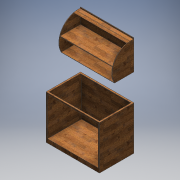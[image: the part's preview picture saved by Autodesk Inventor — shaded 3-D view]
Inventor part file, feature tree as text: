
AUTODESK INVENTOR PART (.ipt)
format: ipt  version: 2016 (Build 200138000, 138)  size: 333,312 bytes
history: native  units: mm
features: extrude x13, sketch x12, projected_geometry x9, plane x3
ambient origin geometry x8: Origin, YZ Plane, XZ Plane, XY Plane, X Axis, Y Axis, Z Axis, Center Point
bodies: Solid1 (feature_tree)
feature tree (37):
  extrude  "Extrusion1"  Depth=10.0mm
  extrude  "Extrusion2"  Depth=80.0mm
  extrude  "Extrusion3"  Depth=30.0mm
  extrude  "Extrusion4"  Depth=30.0mm
  plane  "Work Plane1"
  extrude  "Extrusion5"  Depth=10.0mm
  extrude  "Extrusion6"  Depth=10.0mm
  extrude  "Extrusion7"  Depth=10.0mm
  extrude  "Extrusion9"  TaperAngle=0.0deg  [1 undecoded]
  plane  "Work Plane2"
  extrude  "Extrusion11"  Depth=30.0mm
  extrude  "Extrusion13"  Depth=700.0mm TaperAngle=0.0deg
  plane  "Work Plane3"
  extrude  "Extrusion14"  TaperAngle=0.0deg  [1 undecoded]
  extrude  "Extrusion15"  Depth=10.0mm
  extrude  "Extrusion16"  TaperAngle=0.0deg  [1 undecoded]
  sketch  "Sketch1"  dims[d3=0.0mm d5=10.0mm]
  sketch  "Sketch2"  dims[d6=10.0mm d7=80.0mm]
  projected_geometry  "Projected Loop1"
  sketch  "Sketch3"  dims[d9=0.0mm d10=30.0mm]
  projected_geometry  "Projected Loop2"
  sketch  "Sketch4"  dims[d11=400.0mm d12=0.0mm d13=30.0mm]
  projected_geometry  "Projected Loop3"
  projected_geometry  "Projected Loop4"
  projected_geometry  "Projected Loop5"
  sketch  "Sketch5"  dims[d14=30.0mm d15=10.0mm]
  sketch  "Sketch6"  dims[d16=0.0mm d18=10.0mm]
  projected_geometry  "Projected Loop6"
  sketch  "Sketch7"  dims[d19=0.0mm d20=10.0mm]
  projected_geometry  "Projected Loop7"
  projected_geometry  "Projected Loop9"
  sketch  "Sketch12"  dims[d21=10.0mm d23=0.0mm]
  sketch  "Sketch14"  dims[d24=30.0mm d25=30.0mm]
  sketch  "Sketch15"  dims[d26=30.0mm d27=700.0mm d28=0.0mm]
  sketch  "Sketch16"  dims[d33=10.0mm d34=0.0mm]
  sketch  "Sketch17"  dims[d40=280.0mm d41=10.0mm d42=0.0mm d47=890.0mm d48=0.0mm d54=-30.0mm d55=10.0mm d56=0.0mm d57=10.0mm d58=10.0mm d59=10.0mm d60=0.0mm d61=400.0mm d62=400.0mm d63=10.0mm d64=0.0mm]
  projected_geometry  "Projected Loop12"
note: 3 required parameter values undecoded (feature->parameter linkage not recoverable at this tier; creation-order binding heuristic only, values carry confidence <= 0.55)
